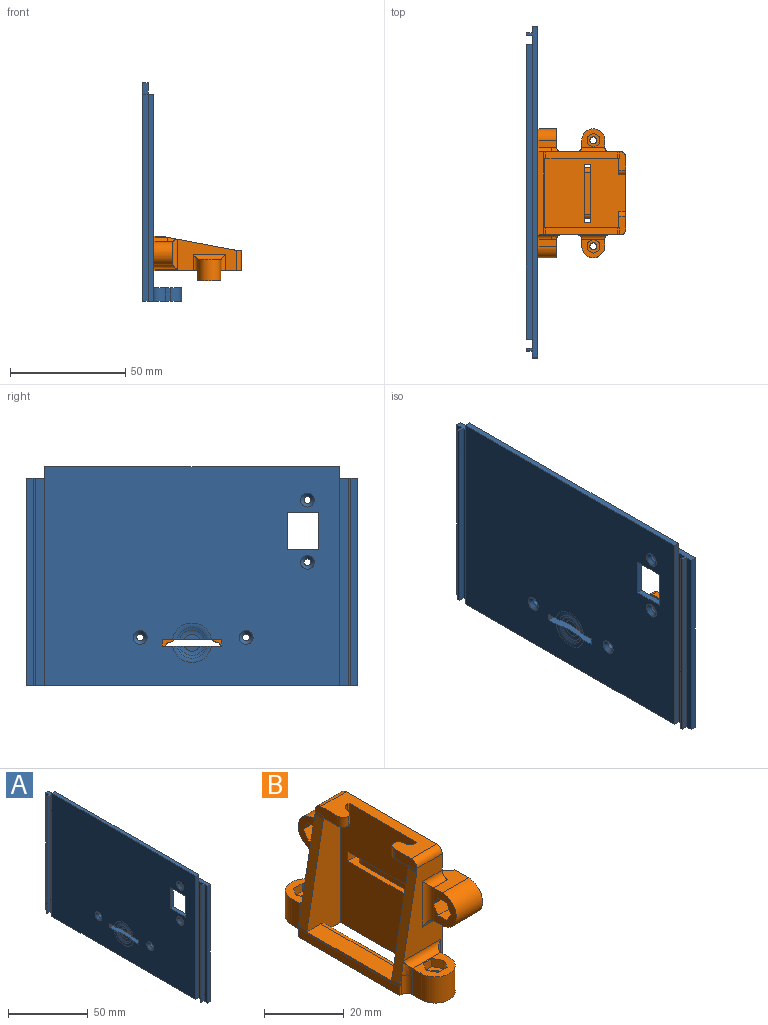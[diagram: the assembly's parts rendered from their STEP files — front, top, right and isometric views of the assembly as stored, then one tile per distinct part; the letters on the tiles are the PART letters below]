
ASSEMBLY  parts=2 mates=1
PART A: 71 faces, bbox 17.2x144.2x95.2 mm
  f0: plane 128x95mm, normal (-1,0,0), area 11571.8mm2, adj f2,f3,f4,f5,f8,f9,f10,f11
  f1: plane 144x90mm, normal (1,0,0), area 12042.2mm2, adj f15,f17,f21,f24,f25,f30,f32,f41
  f2: plane 13.5x2.5mm, normal (0,0,-1), area 33.8mm2, adj f0,f3,f5,f58
  f3: plane 16.1x2.5mm, normal (0,1,0), area 40.3mm2, adj f0,f2,f4,f58
  f4: plane 13.5x2.5mm, normal (0,0,1), area 33.8mm2, adj f0,f3,f5,f58
  f5: plane 16.1x2.5mm, normal (0,-1,0), area 40.3mm2, adj f0,f2,f4,f58
  f6: cylinder r=1.5mm len=3mm, axis (1,0,0), area 9.4mm2, adj f39,f58
  f7: cylinder r=1.5mm len=3mm, axis (1,0,0), area 9.4mm2, adj f40,f58
  f8: plane 26.15x4.15mm, normal (0,0,-1), area 92.2mm2, adj f0,f9,f11,f45,f60,f62,f63,f66
  f9: plane 4x3mm, normal (0,1,0), area 12mm2, adj f0,f8,f10,f45
  f10: plane 26.15x4.15mm, normal (0,0,1), area 92.2mm2, adj f0,f9,f11,f45,f59,f61,f64,f65
  f11: plane 4x3mm, normal (0,-1,0), area 12mm2, adj f0,f8,f10,f45
  f12: plane 90x4mm, normal (-1,0,0), area 360mm2, adj f15,f17,f28,f36
  f13: plane 90x4mm, normal (-1,0,0), area 360mm2, adj f15,f17,f27,f34
  f14: plane 128x2.5mm, normal (0,0,1), area 320.1mm2, adj f0,f16,f27,f28
  f15: plane 144x5mm, normal (0,0,1), area 364.9mm2, adj f1,f12,f13,f16,f29,f30,f31,f32
  f16: plane 128x5mm, normal (1,0,0), area 640mm2, adj f14,f15,f27,f28
  f17: plane 144x17mm, normal (0,0,-1), area 857.9mm2, adj f0,f1,f12,f13,f18,f19,f20,f22
  f18: plane 6x2mm, normal (0,1,0), area 12mm2, adj f17,f21,f22,f25
  f19: plane 6x2mm, normal (0,-1,0), area 12mm2, adj f17,f21,f23,f24
  f20: plane 6x5mm, normal (1,0,0), area 30mm2, adj f17,f21,f22,f23
  f21: plane 25x12mm, normal (0,0,1), area 172.9mm2, adj f1,f18,f19,f20,f22,f23,f24,f25
  f22: cylinder r=5mm len=6mm, axis (0,0,-1), area 47.1mm2, adj f17,f18,f20,f21
  f23: cylinder r=5mm len=6mm, axis (0,0,-1), area 47.1mm2, adj f17,f19,f20,f21
  f24: cylinder r=5mm len=6mm, axis (0,0,1), area 47.1mm2, adj f1,f17,f19,f21
  f25: cylinder r=5mm len=6mm, axis (0,0,1), area 47.1mm2, adj f1,f17,f18,f21
  f26: cylinder r=1.5mm len=6mm, axis (0,0,-1), area 56.5mm2, adj f17,f21
  f27: plane 95x2.5mm, normal (0,1,0), area 237.5mm2, adj f0,f13,f14,f16,f17
  f28: plane 95x2.5mm, normal (0,-1,0), area 237.5mm2, adj f0,f12,f14,f16,f17
  f29: plane 90x3mm, normal (-1,0,0), area 270mm2, adj f15,f17,f30,f33
  f30: plane 90x2.5mm, normal (0,1,0), area 225mm2, adj f1,f15,f17,f29
  f31: plane 90x3mm, normal (-1,0,0), area 270mm2, adj f15,f17,f32,f37
  f32: plane 90x2.5mm, normal (0,-1,0), area 225mm2, adj f1,f15,f17,f31
  f33: plane 90x2.5mm, normal (0,1,0), area 225mm2, adj f15,f17,f29,f35
  f34: plane 90x2.5mm, normal (0,-1,0), area 225mm2, adj f13,f15,f17,f35
  f35: plane 90x1mm, normal (-1,0,0), area 90mm2, adj f15,f17,f33,f34
  f36: plane 90x2.5mm, normal (0,1,0), area 225mm2, adj f12,f15,f17,f38
  f37: plane 90x2.5mm, normal (0,-1,0), area 225mm2, adj f15,f17,f31,f38
  f38: plane 90x1mm, normal (-1,0,0), area 90mm2, adj f15,f17,f36,f37
  f39: cone r=3mm half-angle=45deg, axis (-1,0,0), area 30mm2, adj f0,f6
  f40: cone r=3mm half-angle=45deg, axis (-1,0,0), area 30mm2, adj f0,f7
  f41: plane 30x1mm, normal (0,0,-1), area 30mm2, adj f1,f42,f44,f45
  f42: plane 4.2x1mm, normal (0,1,0), area 4.2mm2, adj f1,f41,f43,f45
  f43: plane 30x1mm, normal (0,0,1), area 30mm2, adj f1,f42,f44,f45
  f44: plane 4.2x1mm, normal (0,-1,0), area 4.2mm2, adj f1,f41,f43,f45
  f45: plane 30x4.2mm, normal (1,0,0), area 48mm2, adj f8,f9,f10,f11,f41,f42,f43,f44
  f46: plane 2.5x2.5mm, normal (0,1,0), area 6.2mm2, adj f1,f47,f57,f58
  f47: cylinder r=5.1mm len=10.2mm, axis (1,0,0), area 40.1mm2, adj f1,f46,f48,f58
  f48: plane 2.5x2.5mm, normal (0,-1,0), area 6.2mm2, adj f1,f47,f49,f58
  f49: plane 6.5x2.5mm, normal (0,0,1), area 16.3mm2, adj f1,f48,f50,f58
  f50: plane 22x2.5mm, normal (0,-1,0), area 55mm2, adj f1,f49,f51,f58
  f51: plane 6.5x2.5mm, normal (0,0,-1), area 16.3mm2, adj f1,f50,f52,f58
  f52: plane 2.5x2.5mm, normal (0,-1,0), area 6.3mm2, adj f1,f51,f53,f58
  f53: cylinder r=5.1mm len=10.2mm, axis (1,0,0), area 40.1mm2, adj f1,f52,f54,f58
  f54: plane 2.5x2.5mm, normal (0,1,0), area 6.3mm2, adj f1,f53,f55,f58
  f55: plane 5.8x2.5mm, normal (0,0,-1), area 14.5mm2, adj f1,f54,f56,f58
  f56: plane 22x2.5mm, normal (0,1,0), area 55mm2, adj f1,f55,f57,f58
  f57: plane 5.8x2.5mm, normal (0,0,1), area 14.5mm2, adj f1,f46,f56,f58
  f58: plane 37.2x22.5mm, normal (1,0,0), area 396.2mm2, adj f2,f3,f4,f5,f6,f7,f46,f47
  f59: plane 6.6x2.13mm, normal (-1,0,0), area 10.1mm2, adj f10,f64
  f60: plane 6.6x2.13mm, normal (-1,0,0), area 10.1mm2, adj f8,f63
  f61: cone r=1.6mm half-angle=71.6deg, axis (-1,0,0), area 19.6mm2, adj f10,f64,f65
  f62: cone r=1.6mm half-angle=71.6deg, axis (-1,0,0), area 19.6mm2, adj f8,f63,f66
  f63: torus R=3.63mm, axis (-1,0,0), area 21.7mm2, adj f8,f60,f62
  f64: torus R=3.63mm, axis (-1,0,0), area 21.7mm2, adj f10,f59,f61
  f65: torus R=8.57mm, axis (1,0,0), area 40.3mm2, adj f0,f10,f61
  f66: torus R=8.57mm, axis (1,0,0), area 40.3mm2, adj f0,f8,f62
  f67: cylinder r=1.5mm len=3.5mm, axis (1,0,0), area 33mm2, adj f1,f70
  f68: cylinder r=1.5mm len=3.5mm, axis (1,0,0), area 33mm2, adj f1,f69
  f69: cone r=3mm half-angle=45deg, axis (-1,0,0), area 30mm2, adj f0,f68
  f70: cone r=3mm half-angle=45deg, axis (-1,0,0), area 30mm2, adj f0,f67
PART B: 109 faces, bbox 19.5x56.2x38.2 mm
  f0: cylinder r=1.5mm len=5.3mm, axis (1,0,0), area 50mm2, adj f83,f98
  f1: cylinder r=1.5mm len=5.3mm, axis (1,0,0), area 50mm2, adj f78,f85
  f2: plane 38x30mm, normal (-1,0,0), area 1047mm2, adj f6,f7,f8,f9,f11,f17,f38,f39
  f3: plane 40x38mm, normal (1,0,0), area 1280.7mm2, adj f6,f14,f15,f17,f63,f64,f68,f69
  f4: plane 5.67x0.5mm, normal (0,-1,0), area 2.2mm2, adj f16,f17,f44,f59,f66
  f5: plane 5.67x0.5mm, normal (0,1,0), area 2.2mm2, adj f16,f17,f43,f57,f66
  f6: plane 32x9mm, normal (0,0,1), area 170.3mm2, adj f2,f3,f10,f38,f39,f40,f49,f50
  f7: plane 35.46x11.98mm, normal (0,-1,0), area 302.7mm2, adj f2,f10,f11,f17,f41,f42,f43,f45
  f8: plane 35.46x11.98mm, normal (0,1,0), area 302.7mm2, adj f2,f9,f17,f40,f41,f42,f44,f45
  f9: plane 6.98x6mm, normal (0,0,-1), area 31.1mm2, adj f2,f8,f39,f40,f52,f53,f54
  f10: plane 8x3mm, normal (-1,0,0), area 21.7mm2, adj f6,f7,f11,f15,f49,f63,f67
  f11: plane 6.98x6mm, normal (0,0,-1), area 31.1mm2, adj f2,f7,f10,f38,f49,f50,f51
  f12: cylinder r=1.5mm len=5.5mm, axis (0,0,-1), area 51.8mm2, adj f17,f31
  f13: cylinder r=1.5mm len=5.5mm, axis (0,0,-1), area 51.8mm2, adj f17,f30
  f14: plane 36x13.69mm, normal (0,-1,0), area 199.6mm2, adj f3,f17,f40,f44,f61,f62,f64,f65
  f15: plane 36x13.69mm, normal (0,1,0), area 199.6mm2, adj f3,f10,f17,f43,f55,f56,f63,f67
  f16: plane 36x2.54mm, normal (-1,0,0), area 91.3mm2, adj f4,f5,f17,f66
  f17: plane 56x15mm, normal (0,0,-1), area 581.8mm2, adj f2,f3,f4,f5,f7,f8,f12,f13
  f18: plane 8x3.05mm, normal (-1,0,0), area 24mm2, adj f17,f20,f47,f59,f60,f61
  f19: plane 8x3mm, normal (1,0,0), area 24mm2, adj f17,f20,f47,f62
  f20: plane 10x8mm, normal (0,0,1), area 44mm2, adj f18,f19,f24,f25,f26,f27,f28,f29
  f21: plane 8x3.05mm, normal (-1,0,0), area 24mm2, adj f17,f23,f46,f56,f57,f58
  f22: plane 8x3mm, normal (1,0,0), area 24mm2, adj f17,f23,f46,f55
  f23: plane 10x8mm, normal (0,0,1), area 44mm2, adj f21,f22,f32,f33,f34,f35,f36,f37
  f24: plane 3.12x2.5mm, normal (0,1,0), area 7.8mm2, adj f20,f25,f29,f30
  f25: plane 2.7x2.5mm, normal (-0.87,0.5,0), area 7.8mm2, adj f20,f24,f26,f30
  f26: plane 2.7x2.5mm, normal (-0.87,-0.5,0), area 7.8mm2, adj f20,f25,f27,f30
  f27: plane 3.12x2.5mm, normal (0,-1,0), area 7.8mm2, adj f20,f26,f28,f30
  f28: plane 2.7x2.5mm, normal (0.87,-0.5,0), area 7.8mm2, adj f20,f27,f29,f30
  f29: plane 2.7x2.5mm, normal (0.87,0.5,0), area 7.8mm2, adj f20,f24,f28,f30
  f30: plane 6.24x5.4mm, normal (0,0,1), area 18.2mm2, adj f13,f24,f25,f26,f27,f28,f29
  f31: plane 6.24x5.4mm, normal (0,0,1), area 18.2mm2, adj f12,f32,f33,f34,f35,f36,f37
  f32: plane 3.12x2.5mm, normal (0,1,0), area 7.8mm2, adj f23,f31,f33,f37
  f33: plane 2.7x2.5mm, normal (-0.87,0.5,0), area 7.8mm2, adj f23,f31,f32,f34
  f34: plane 2.7x2.5mm, normal (-0.87,-0.5,0), area 7.8mm2, adj f23,f31,f33,f35
  f35: plane 3.12x2.5mm, normal (0,-1,0), area 7.8mm2, adj f23,f31,f34,f36
  f36: plane 2.7x2.5mm, normal (0.87,-0.5,0), area 7.8mm2, adj f23,f31,f35,f37
  f37: plane 2.7x2.5mm, normal (0.87,0.5,0), area 7.8mm2, adj f23,f31,f32,f36
  f38: plane 3x0.5mm, normal (0,-1,0), area 1.5mm2, adj f2,f6,f11,f50
  f39: plane 3x0.5mm, normal (0,1,0), area 1.5mm2, adj f2,f6,f9,f52
  f40: plane 8x3mm, normal (-1,0,0), area 21.7mm2, adj f6,f8,f9,f14,f53,f64,f65
  f41: plane 30x4.95mm, normal (0,0,1), area 148.5mm2, adj f7,f8,f48,f66
  f42: plane 30x1mm, normal (1,0,0), area 30mm2, adj f7,f8,f17,f45
  f43: plane 31.14x5.88mm, normal (-0.98,0,0.18), area 94.9mm2, adj f5,f7,f15,f58,f66,f67
  f44: plane 31.24x5.98mm, normal (-0.98,0,0.18), area 94.9mm2, adj f4,f8,f14,f60,f65,f66
  f45: plane 30x1.41mm, normal (0.71,0,0.71), area 60mm2, adj f7,f8,f42,f48
  f46: cylinder r=5mm len=10mm, axis (0,0,-1), area 125.7mm2, adj f17,f21,f22,f23
  f47: cylinder r=5mm len=10mm, axis (0,0,-1), area 125.7mm2, adj f17,f18,f19,f20
  f48: cylinder r=2mm len=30mm, axis (0,1,0), area 47.1mm2, adj f7,f8,f41,f45
  f49: cylinder r=2mm len=3mm, axis (0,0,1), area 8.7mm2, adj f6,f10,f11,f51
  f50: cylinder r=2mm len=3mm, axis (0,0,1), area 9.4mm2, adj f6,f11,f38,f51
  f51: cylinder r=2mm len=3mm, axis (0,0,-1), area 8.7mm2, adj f6,f11,f49,f50
  f52: cylinder r=2mm len=3mm, axis (0,0,-1), area 9.4mm2, adj f6,f9,f39,f54
  f53: cylinder r=2mm len=3mm, axis (0,0,-1), area 8.7mm2, adj f6,f9,f40,f54
  f54: cylinder r=2mm len=3mm, axis (0,0,1), area 8.7mm2, adj f6,f9,f52,f53
  f55: cylinder r=2mm len=10mm, axis (0,0,1), area 28.3mm2, adj f15,f17,f22,f56
  f56: cylinder r=2mm len=13.2mm, axis (1,0,0), area 35.5mm2, adj f15,f21,f23,f55,f58
  f57: cylinder r=2mm len=5.67mm, axis (0,0,1), area 17.8mm2, adj f5,f17,f21,f58
  f58: bspline ~6.38x2.19mm, area 9.4mm2, adj f21,f43,f56,f57
  f59: cylinder r=2mm len=5.67mm, axis (0,0,-1), area 17.8mm2, adj f4,f17,f18,f60
  f60: bspline ~8.33x2.64mm, area 9.5mm2, adj f18,f44,f59,f61
  f61: cylinder r=2mm len=13.2mm, axis (-1,0,0), area 35.5mm2, adj f14,f18,f20,f60,f62
  f62: cylinder r=2mm len=10mm, axis (0,0,-1), area 28.3mm2, adj f14,f17,f19,f61
  f63: cylinder r=2mm len=9mm, axis (1,0,0), area 28.3mm2, adj f3,f6,f10,f15
  f64: cylinder r=2mm len=9mm, axis (-1,0,0), area 28.3mm2, adj f3,f6,f14,f40
  f65: cylinder r=5mm len=3mm, axis (0,1,0), area 2.8mm2, adj f8,f14,f40,f44
  f66: cylinder r=5mm len=36mm, axis (0,1,0), area 19.5mm2, adj f4,f5,f7,f8,f16,f41,f43,f44
  f67: cylinder r=5mm len=3mm, axis (0,1,0), area 2.8mm2, adj f7,f10,f15,f43
  f68: plane 3x3mm, normal (0,-1,0), area 9mm2, adj f2,f3,f69,f71
  f69: plane 25x3mm, normal (0,0,-1), area 43.5mm2, adj f2,f3,f68,f70,f72,f73,f74
  f70: plane 3x3mm, normal (0,1,0), area 9mm2, adj f2,f3,f69,f71
  f71: plane 25x3mm, normal (0,0,1), area 43.5mm2, adj f2,f3,f68,f70,f72,f73,f74
  f72: plane 18.13x3mm, normal (-1,0,0), area 54.4mm2, adj f69,f71,f73,f74
  f73: cylinder r=2mm len=3mm, axis (0,0,1), area 7.9mm2, adj f3,f69,f71,f72
  f74: cylinder r=2mm len=3mm, axis (0,0,1), area 7.9mm2, adj f3,f69,f71,f72
  f75: plane 10x0.3mm, normal (0,1,0), area 3mm2, adj f76,f77,f78,f108
  f76: plane 9.3x9mm, normal (0,0,1), area 44.5mm2, adj f3,f75,f78,f79,f100,f106,f108
  f77: plane 9.3x9mm, normal (0,0,-1), area 44.5mm2, adj f3,f75,f78,f79,f100,f104,f108
  f78: plane 10x10mm, normal (1,0,0), area 82.2mm2, adj f1,f75,f76,f77,f100
  f79: plane 10x8mm, normal (-1,0,0), area 44mm2, adj f76,f77,f86,f87,f88,f89,f90,f91
  f80: plane 10x0.3mm, normal (0,-1,0), area 3mm2, adj f81,f82,f83,f107
  f81: plane 9.3x9mm, normal (0,0,1), area 44.5mm2, adj f3,f80,f83,f84,f99,f101,f107
  f82: plane 9.3x9mm, normal (0,0,-1), area 44.5mm2, adj f3,f80,f83,f84,f99,f103,f107
  f83: plane 10x10mm, normal (1,0,0), area 82.2mm2, adj f0,f80,f81,f82,f99
  f84: plane 10x8mm, normal (-1,0,0), area 44mm2, adj f81,f82,f92,f93,f94,f95,f96,f97
  f85: plane 6.24x5.4mm, normal (-1,0,0), area 18.2mm2, adj f1,f86,f87,f88,f89,f90,f91
  f86: plane 4x3.12mm, normal (0,0,-1), area 12.5mm2, adj f79,f85,f87,f91
  f87: plane 4x2.7mm, normal (0,-0.87,-0.5), area 12.5mm2, adj f79,f85,f86,f88,f105
  f88: plane 4x2.7mm, normal (0,-0.87,0.5), area 12.5mm2, adj f79,f85,f87,f89,f105
  f89: plane 4x3.12mm, normal (0,0,1), area 12.5mm2, adj f79,f85,f88,f90
  f90: plane 4x2.7mm, normal (0,0.87,0.5), area 12.5mm2, adj f79,f85,f89,f91
  f91: plane 4x2.7mm, normal (0,0.87,-0.5), area 12.5mm2, adj f79,f85,f86,f90
  f92: plane 4x3.12mm, normal (0,0,-1), area 12.5mm2, adj f84,f93,f97,f98
  f93: plane 4x2.7mm, normal (0,-0.87,-0.5), area 12.5mm2, adj f84,f92,f94,f98
  f94: plane 4x2.7mm, normal (0,-0.87,0.5), area 12.5mm2, adj f84,f93,f95,f98
  f95: plane 4x3.12mm, normal (0,0,1), area 12.5mm2, adj f84,f94,f96,f98
  f96: plane 4x2.7mm, normal (0,0.87,0.5), area 12.5mm2, adj f84,f95,f97,f98,f102
  f97: plane 4x2.7mm, normal (0,0.87,-0.5), area 12.5mm2, adj f84,f92,f96,f98,f102
  f98: plane 6.24x5.4mm, normal (-1,0,0), area 18.2mm2, adj f0,f92,f93,f94,f95,f96,f97
  f99: cylinder r=5mm len=10mm, axis (-1,0,0), area 146.1mm2, adj f81,f82,f83,f84
  f100: cylinder r=5mm len=10mm, axis (-1,0,0), area 146.1mm2, adj f76,f77,f78,f79
  f101: cylinder r=2mm len=7mm, axis (1,0,0), area 18.8mm2, adj f3,f15,f81,f102
  f102: cylinder r=2mm len=14mm, axis (0,0,-1), area 36mm2, adj f15,f84,f96,f97,f101,f103
  f103: cylinder r=2mm len=7mm, axis (1,0,0), area 18.8mm2, adj f3,f15,f82,f102
  f104: cylinder r=2mm len=7mm, axis (-1,0,0), area 18.8mm2, adj f3,f14,f77,f105
  f105: cylinder r=2mm len=14mm, axis (0,0,-1), area 36mm2, adj f14,f79,f87,f88,f104,f106
  f106: cylinder r=2mm len=7mm, axis (-1,0,0), area 18.8mm2, adj f3,f14,f76,f105
  f107: plane 10x4mm, normal (0.71,-0.71,0), area 56.6mm2, adj f3,f80,f81,f82
  f108: plane 10x4mm, normal (0.71,0.71,0), area 56.6mm2, adj f3,f75,f76,f77
PLACE A t=(39.67,-5.42,12.53)mm fixed
PLACE B rot(axis=(0,1,0),90deg) t=(-87.83,-5.92,38.33)mm
MATE fastened B.f13 <-> A.f69  axis (-1,0,0) through (-87.83,-28.92,38.33)mm
